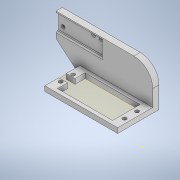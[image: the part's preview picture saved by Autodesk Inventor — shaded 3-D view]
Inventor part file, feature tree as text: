
AUTODESK INVENTOR PART (.ipt)
format: ipt  version: 2021 (Build 250183000, 183)  size: 245,248 bytes
history: native  units: mm
features: sketch x9, extrude x8, other x1, plane x1, fillet x1, chamfer x1
ambient origin geometry x8: Origin, YZ Plane, XZ Plane, XY Plane, X Axis, Y Axis, Z Axis, Center Point
bodies: Body1 (feature_tree)
feature tree (21):
  other  "Sólido1"
  plane  "Plano de trabajo1"
  extrude  "Extrusión2"  Depth=5.0mm
  sketch  "Boceto3"  dims[d10=7.0mm d11=2.0mm]
  extrude  "Extrusión3"  Depth=2.0mm
  extrude  "Extrusión4"  Depth=3.0mm
  extrude  "Extrusión5"  Depth=7.0mm
  extrude  "Extrusión6"  Depth=1.0mm
  extrude  "Extrusión7"  Depth=4.0mm
  extrude  "Extrusión9"  Depth=3.0mm
  extrude  "Extrusión10"  Depth=14.1mm
  fillet  "Empalme1"  Radius=4.0mm
  chamfer  "Chaflán1"  Distance=10.5mm
  sketch  "Boceto2"  dims[d8=5.0mm d9=5.0mm]
  sketch  "Boceto4"  dims[d12=3.0mm d13=3.0mm]
  sketch  "Boceto5"  dims[d14=1.0mm d15=7.0mm]
  sketch  "Boceto6"  dims[d16=1.0mm d17=1.0mm]
  sketch  "Boceto7"  dims[d18=4.0mm d19=4.0mm]
  sketch  "Boceto8"  dims[d20=4.0mm d21=0.0mm d22=3.0mm]
  sketch  "Boceto10"  dims[d23=3.0mm d24=14.1mm d25=4.0mm]
  sketch  "Boceto11"  dims[d26=14.0mm d27=10.5mm d28=10.1mm d29=23.0mm d30=10.0mm d31=0.1mm d32=0.1mm d33=13.0mm d34=10.1mm d35=2.0mm d36=2.0mm d38=0.05mm d39=3.0mm d40=6.0mm d41=3.0mm d42=5.0mm d43=0.0mm d44=10.5mm d45=2.05mm d46=3.0mm d47=6.0mm d48=3.0mm d49=3.0mm d50=0.0mm d51=4.0mm d52=0.0mm d53=2.0mm d54=0.0mm d55=19.1mm d56=0.0mm d62=3.711mm d63=4.0mm d64=3.0mm d65=19.1mm d66=0.0mm d67=19.1mm d68=0.0mm d69=15.0mm d70=1.0mm d71=2.0mm d72=45.0deg]
